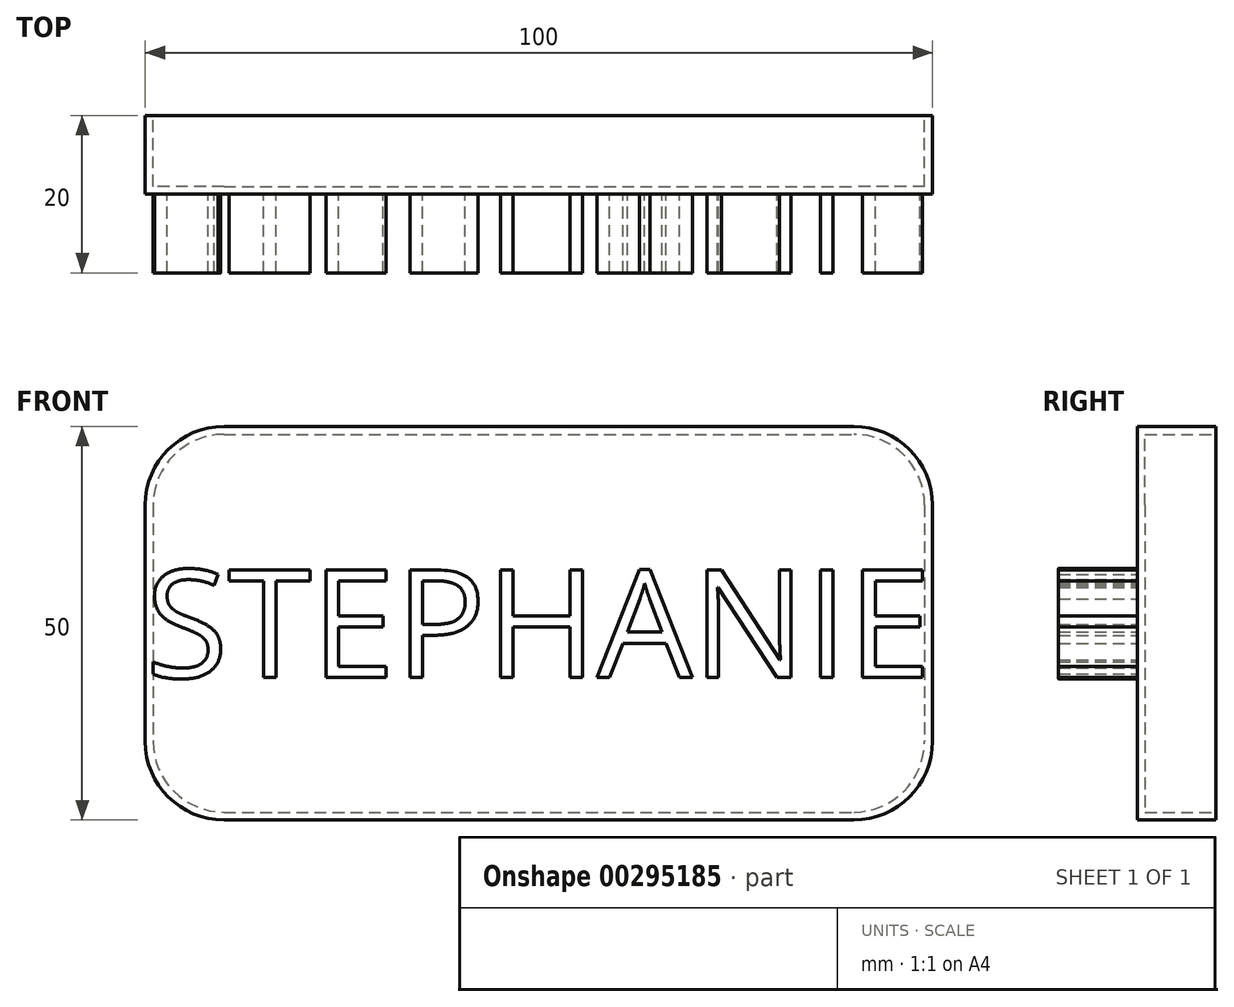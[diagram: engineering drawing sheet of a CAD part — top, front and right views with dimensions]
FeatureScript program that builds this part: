
annotation { "Feature Type Name" : "Feature", "Feature Type Description" : "" }
export const myFeature = defineFeature(function(context is Context, id is Id, definition is map)
    precondition{}
    {
        {
            var Q0;
            Q0=qCreatedBy(makeId("Front.planeOp"),FACE);
            var sketch = newSketch(context, id + "F0", { "sketchPlane" : qUnion([Q0])});
            skLineSegment(sketch, "E0.bottom", {"start": v(-40, 25) * mm, "end": v(40, 25) * mm});
            skLineSegment(sketch, "E0.top", {"start": v(-40, -25) * mm, "end": v(40, -25) * mm});
            skLineSegment(sketch, "E0.left", {"start": v(-50, 15) * mm, "end": v(-50, -15) * mm});
            skLineSegment(sketch, "E0.right", {"start": v(50, 15) * mm, "end": v(50, -15) * mm});
            skPoint(sketch, "E0.middle", {"position": v(0, 0) * mm});
            skPoint(sketch, "E1.visualSharp", {"position": v(-50, 25) * mm});
            skArc(sketch, "E1.filletArc", {"start": v(-40, 25) * mm, "mid": v(-47.07, 22.07) * mm, "end": v(-50, 15) * mm});
            skPoint(sketch, "E2.visualSharp", {"position": v(50, 25) * mm});
            skArc(sketch, "E2.filletArc", {"start": v(50, 15) * mm, "mid": v(47.07, 22.07) * mm, "end": v(40, 25) * mm});
            skPoint(sketch, "E3.visualSharp", {"position": v(50, -25) * mm});
            skArc(sketch, "E3.filletArc", {"start": v(40, -25) * mm, "mid": v(47.07, -22.07) * mm, "end": v(50, -15) * mm});
            skPoint(sketch, "E4.visualSharp", {"position": v(-50, -25) * mm});
            skArc(sketch, "E4.filletArc", {"start": v(-50, -15) * mm, "mid": v(-47.07, -22.07) * mm, "end": v(-40, -25) * mm});
            skSolve(sketch);
        }
        {
            var Q0;
            Q0 = qSketchRegion(id + "F0", true);
            extrude(context, id + "F1", {"entities" : qUnion([Q0]), "depth" : 10 * mm});
        }
        {
            var Q0;
            Q0=makeQuery(id+"F1.opExtrude","CAP_FACE",FACE,{"disambiguationData":[OSD([sQuery(id+"F0.wireOp",EDGE,"E0.bottom"),sQuery(id+"F0.wireOp",EDGE,"E0.top"),sQuery(id+"F0.wireOp",EDGE,"E0.left"),sQuery(id+"F0.wireOp",EDGE,"E0.right"),sQuery(id+"F0.wireOp",EDGE,"E1.filletArc"),sQuery(id+"F0.wireOp",EDGE,"E2.filletArc"),sQuery(id+"F0.wireOp",EDGE,"E3.filletArc"),sQuery(id+"F0.wireOp",EDGE,"E4.filletArc")])],"isStart":true});
            shell(context, id + "F2", {"entities" : qUnion([Q0]), "thickness" : 1 * mm});
        }
        {
            var Q0;
            Q0=makeQuery(id+"F1.opExtrude","CAP_FACE",FACE,{"disambiguationData":[OSD([sQuery(id+"F0.wireOp",EDGE,"E0.bottom"),sQuery(id+"F0.wireOp",EDGE,"E0.top"),sQuery(id+"F0.wireOp",EDGE,"E0.left"),sQuery(id+"F0.wireOp",EDGE,"E0.right"),sQuery(id+"F0.wireOp",EDGE,"E1.filletArc"),sQuery(id+"F0.wireOp",EDGE,"E2.filletArc"),sQuery(id+"F0.wireOp",EDGE,"E3.filletArc"),sQuery(id+"F0.wireOp",EDGE,"E4.filletArc")])],"isStart":false});
            var sketch = newSketch(context, id + "F3", { "sketchPlane" : qUnion([Q0])});
            skText(sketch, "E5", { "text": "STEPHANIE", "fontName": "OpenSans-Regular.ttf"});
            const initialGuessF3  = {"E5": [-0.05, -0.0069, 1, 0, 0.01378]};
            skSetInitialGuess(sketch, initialGuessF3);
            skSolve(sketch);
        }
        {
            var Q0;
            Q0 = qSketchRegion(id + "F3", true);
            extrude(context, id + "F4", {"entities" : qUnion([Q0]), "operationType" : NewBodyOperationType.ADD, "depth" : 10 * mm});
        }
    });
